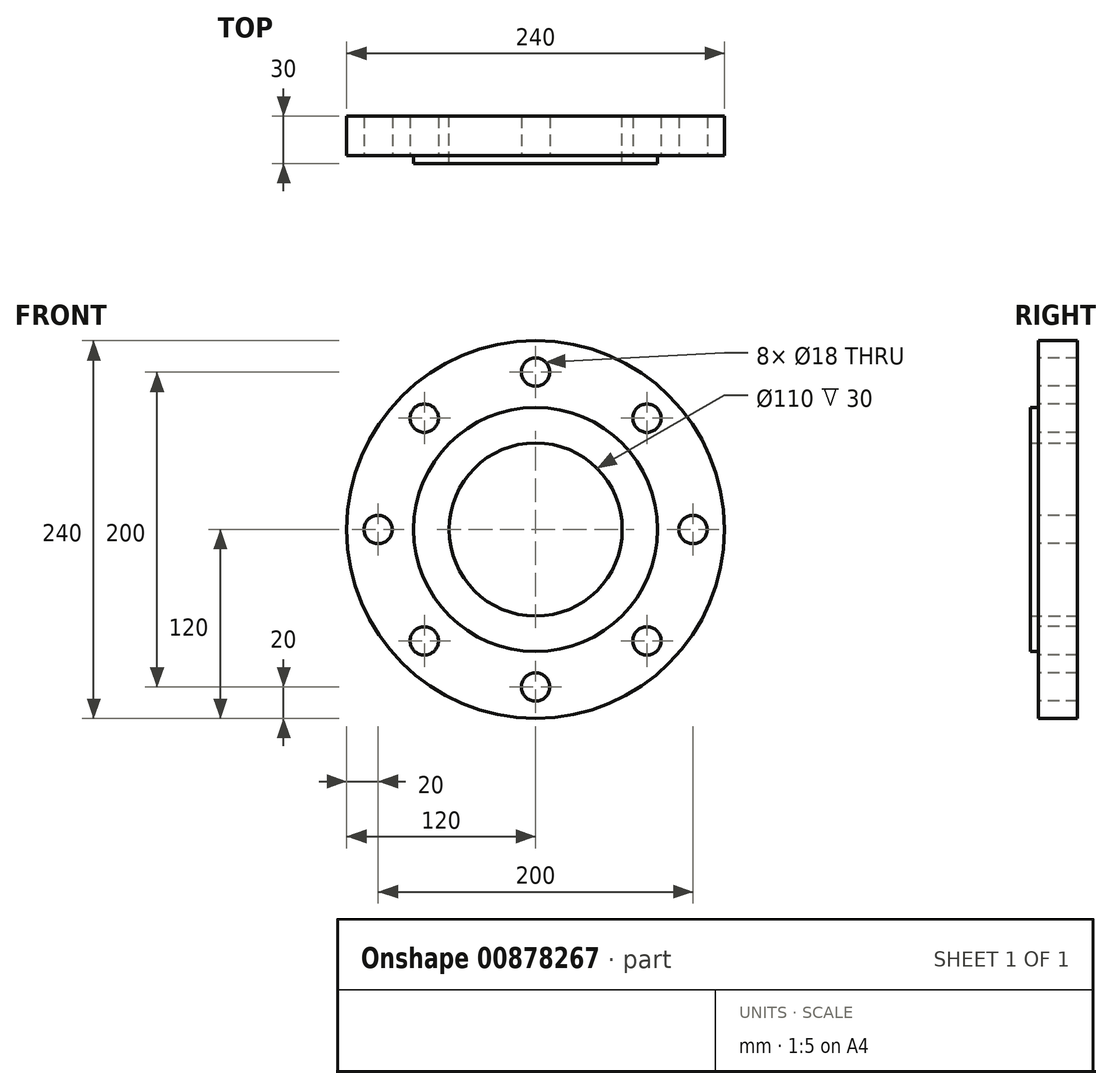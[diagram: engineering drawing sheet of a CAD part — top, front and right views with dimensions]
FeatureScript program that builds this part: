
annotation { "Feature Type Name" : "Feature", "Feature Type Description" : "" }
export const myFeature = defineFeature(function(context is Context, id is Id, definition is map)
    precondition{}
    {
        {
            var Q0;
            Q0=qCreatedBy(makeId("Front.planeOp"),FACE);
            var sketch = newSketch(context, id + "F0", { "sketchPlane" : qUnion([Q0])});
            skCircle(sketch, "E0", {"center": v(0, 0) * mm, "radius": 55 * mm});
            skCircle(sketch, "E1", {"center": v(0, 0) * mm, "radius": 120 * mm});
            skSolve(sketch);
        }
        {
            var Q0;
            Q0=makeQuery(id+"F0.imprint","IMPRINT",FACE,{"disambiguationData":[TD([[makeQuery(id+"F0.imprint","IMPRINT",EDGE,{"derivedFrom":sQuery(id+"F0.wireOp",EDGE,"E0")}),-1.0]])]});
            extrude(context, id + "F1", {"entities" : qUnion([Q0]), "depth" : 25 * mm, "offsetDistance" : 25 * mm});
        }
        {
            var Q0;
            Q0=makeQuery(id+"F1.opExtrude","CAP_FACE",FACE,{"disambiguationData":[OSD([sQuery(id+"F0.wireOp",EDGE,"E0"),sQuery(id+"F0.wireOp",EDGE,"E1")])],"isStart":false});
            var sketch = newSketch(context, id + "F2", { "sketchPlane" : qUnion([Q0])});
            skCircle(sketch, "E2", {"center": v(0, 0) * mm, "radius": 100 * mm});
            skSolve(sketch);
        }
        {
            var Q0;
            Q0=makeQuery(id+"F2.imprint","IMPRINT",FACE,{"disambiguationData":[TD([[makeQuery(id+"F2.imprint","IMPRINT",EDGE,{"derivedFrom":sQuery(id+"F2.wireOp",EDGE,"E2")}),-1.0]])]});
            var sketch = newSketch(context, id + "F3", { "sketchPlane" : qUnion([Q0])});
            skCircle(sketch, "E3", {"center": v(0, 100) * mm, "radius": 9 * mm});
            skCircle(sketch, "E4.1.0", {"center": v(-70.71, 70.71) * mm, "radius": 9 * mm});
            skCircle(sketch, "E4.2.0", {"center": v(-100, 0) * mm, "radius": 9 * mm});
            skCircle(sketch, "E4.3.0", {"center": v(-70.71, -70.71) * mm, "radius": 9 * mm});
            skCircle(sketch, "E4.4.0", {"center": v(0, -100) * mm, "radius": 9 * mm});
            skCircle(sketch, "E4.5.0", {"center": v(70.71, -70.71) * mm, "radius": 9 * mm});
            skCircle(sketch, "E4.6.0", {"center": v(100, 0) * mm, "radius": 9 * mm});
            skCircle(sketch, "E4.7.0", {"center": v(70.71, 70.71) * mm, "radius": 9 * mm});
            skPoint(sketch, "E4.center", {"position": v(0, 0) * mm});
            skSolve(sketch);
        }
        {
            var Q0;
            Q0 = qSketchRegion(id + "F3", true);
            extrude(context, id + "F4", {"entities" : qUnion([Q0]), "operationType" : NewBodyOperationType.REMOVE, "oppositeDirection" : true, "depth" : 25 * mm, "offsetDistance" : 25 * mm});
        }
        {
            var Q0;
            Q0=makeQuery(id+"F2.imprint","IMPRINT",FACE,{"disambiguationData":[TD([[makeQuery(id+"F2.imprint","IMPRINT",EDGE,{"derivedFrom":sQuery(id+"F2.wireOp",EDGE,"E2")}),1.0]])]});
            var sketch = newSketch(context, id + "F5", { "sketchPlane" : qUnion([Q0])});
            skCircle(sketch, "E5", {"center": v(0, 0) * mm, "radius": 77.5 * mm});
            skCircle(sketch, "E6", {"center": v(0, 0) * mm, "radius": 55 * mm});
            skSolve(sketch);
        }
        {
            var Q0;
            Q0=makeQuery(id+"F5.imprint","IMPRINT",FACE,{"disambiguationData":[TD([[makeQuery(id+"F5.imprint","IMPRINT",EDGE,{"derivedFrom":sQuery(id+"F5.wireOp",EDGE,"E5")}),1.0]])]});
            extrude(context, id + "F6", {"entities" : qUnion([Q0]), "operationType" : NewBodyOperationType.ADD, "depth" : 5 * mm, "offsetDistance" : 25 * mm});
        }
    });
